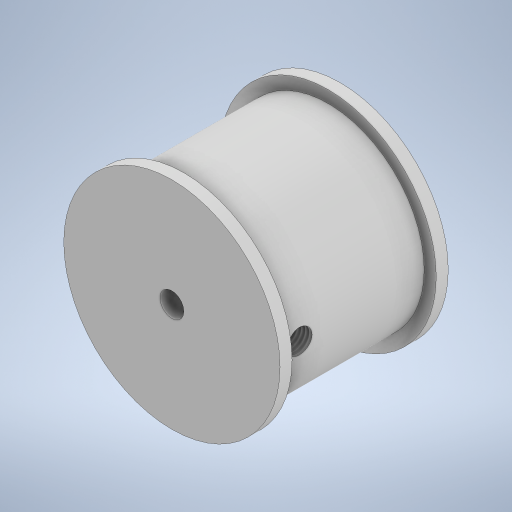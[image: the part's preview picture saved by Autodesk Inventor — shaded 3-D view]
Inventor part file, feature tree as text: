
AUTODESK INVENTOR PART (.ipt)
format: ipt  version: 2024 (Build 280153000, 153)  size: 283,648 bytes
history: native  units: mm
features: sketch x5, extrude x4, other x2, hole x2
ambient origin geometry x8: Origin, YZ Plane, XZ Plane, XY Plane, X Axis, Y Axis, Z Axis, Center Point
bodies: Body1 (feature_tree)
feature tree (13):
  other  "Těleso1"
  sketch  "Náčrt1"
  extrude  "Vysunutí1"  Depth=33.0mm
  hole  "Díra2"  [1 undecoded]
  other  "Závit1"
  extrude  "Vysunutí2"  Depth=21.0mm TaperAngle=0.0deg
  extrude  "Vysunutí3"  Depth=18.0mm TaperAngle=0.0deg
  hole  "Díra1"  [1 undecoded]
  extrude  "Vysunutí4"  Depth=14.5mm TaperAngle=0.0deg
  sketch  "Náčrt2"
  sketch  "Náčrt3"
  sketch  "Náčrt4"
  sketch  "Náčrt5"
note: 2 required parameter values undecoded (feature->parameter linkage not recoverable at this tier; creation-order binding heuristic only, values carry confidence <= 0.55)
